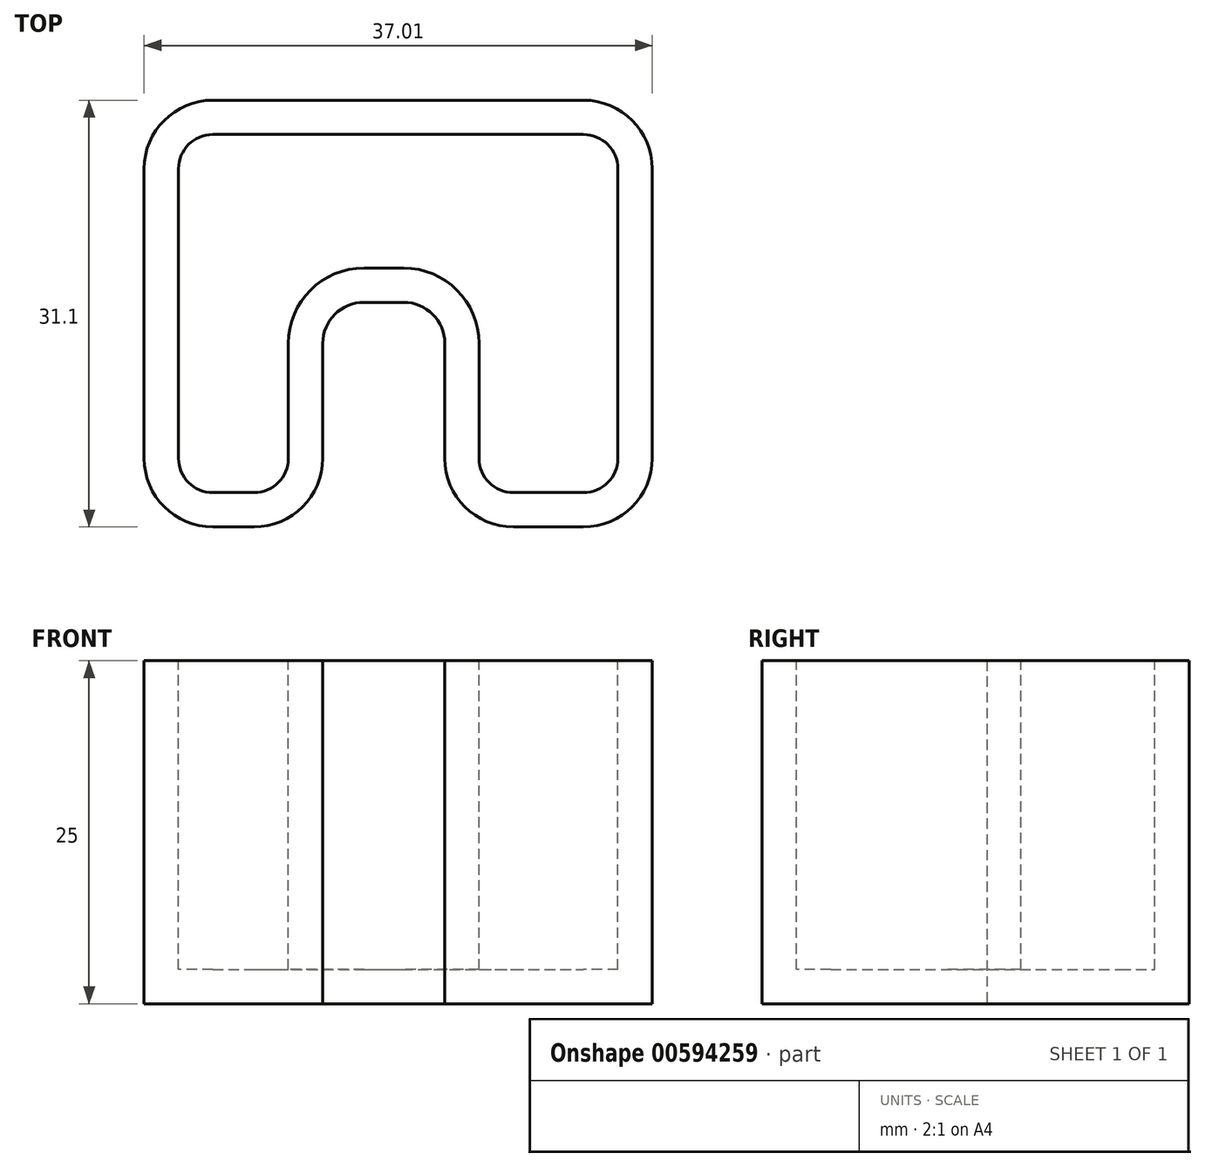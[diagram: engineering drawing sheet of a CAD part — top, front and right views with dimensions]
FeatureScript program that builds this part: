
annotation { "Feature Type Name" : "Feature", "Feature Type Description" : "" }
export const myFeature = defineFeature(function(context is Context, id is Id, definition is map)
    precondition{}
    {
        {
            var Q0;
            Q0=qCreatedBy(makeId("Top.planeOp"),FACE);
            var sketch = newSketch(context, id + "F0", { "sketchPlane" : qUnion([Q0])});
            skLineSegment(sketch, "E0.bottom", {"start": v(5, 0) * mm, "end": v(8, 0) * mm});
            skLineSegment(sketch, "E0.top", {"start": v(5, 31.1) * mm, "end": v(32, 31.1) * mm});
            skLineSegment(sketch, "E0.left", {"start": v(0, 5) * mm, "end": v(0, 26.1) * mm});
            skLineSegment(sketch, "E0.right", {"start": v(37, 5) * mm, "end": v(37, 26.1) * mm});
            skLineSegment(sketch, "E1.top", {"start": v(16, 16.37) * mm, "end": v(18.9, 16.37) * mm});
            skLineSegment(sketch, "E1.left", {"start": v(13, 5) * mm, "end": v(13, 13.37) * mm});
            skLineSegment(sketch, "E1.right", {"start": v(21.9, 5) * mm, "end": v(21.9, 13.37) * mm});
            skLineSegment(sketch, "E2.trimOffspring", {"start": v(26.9, 0) * mm, "end": v(32, 0) * mm});
            skPoint(sketch, "E3.visualSharp", {"position": v(0, 31.1) * mm});
            skArc(sketch, "E3.filletArc", {"start": v(5, 31.1) * mm, "mid": v(1.46, 29.63) * mm, "end": v(0, 26.1) * mm});
            skPoint(sketch, "E4.visualSharp", {"position": v(37, 31.1) * mm});
            skArc(sketch, "E4.filletArc", {"start": v(37, 26.1) * mm, "mid": v(35.54, 29.63) * mm, "end": v(32, 31.1) * mm});
            skPoint(sketch, "E5.visualSharp", {"position": v(37, 0) * mm});
            skArc(sketch, "E5.filletArc", {"start": v(32, 0) * mm, "mid": v(35.54, 1.46) * mm, "end": v(37, 5) * mm});
            skPoint(sketch, "E6.visualSharp", {"position": v(21.9, 0) * mm});
            skArc(sketch, "E6.filletArc", {"start": v(21.9, 5) * mm, "mid": v(23.36, 1.46) * mm, "end": v(26.9, 0) * mm});
            skPoint(sketch, "E7.visualSharp", {"position": v(21.9, 16.37) * mm});
            skArc(sketch, "E7.filletArc", {"start": v(21.9, 13.37) * mm, "mid": v(21.02, 15.49) * mm, "end": v(18.9, 16.37) * mm});
            skPoint(sketch, "E8.visualSharp", {"position": v(0, 0) * mm});
            skArc(sketch, "E8.filletArc", {"start": v(0, 5) * mm, "mid": v(1.46, 1.46) * mm, "end": v(5, 0) * mm});
            skPoint(sketch, "E9.visualSharp", {"position": v(13, 0) * mm});
            skArc(sketch, "E9.filletArc", {"start": v(8, 0) * mm, "mid": v(11.54, 1.46) * mm, "end": v(13, 5) * mm});
            skPoint(sketch, "E10.visualSharp", {"position": v(13, 16.37) * mm});
            skArc(sketch, "E10.filletArc", {"start": v(16, 16.37) * mm, "mid": v(13.89, 15.49) * mm, "end": v(13, 13.37) * mm});
            skSolve(sketch);
        }
        {
            var Q0;
            Q0 = qSketchRegion(id + "F0", true);
            extrude(context, id + "F1", {"entities" : qUnion([Q0]), "depth" : 25 * mm, "offsetDistance" : 25 * mm});
        }
        {
            var Q0;
            Q0=makeQuery(id+"F1.opExtrude","CAP_FACE",FACE,{"disambiguationData":[OSD([sQuery(id+"F0.wireOp",EDGE,"E0.bottom"),sQuery(id+"F0.wireOp",EDGE,"E0.top"),sQuery(id+"F0.wireOp",EDGE,"E0.left"),sQuery(id+"F0.wireOp",EDGE,"E0.right"),sQuery(id+"F0.wireOp",EDGE,"E1.top"),sQuery(id+"F0.wireOp",EDGE,"E1.left"),sQuery(id+"F0.wireOp",EDGE,"E1.right"),sQuery(id+"F0.wireOp",EDGE,"E2.trimOffspring"),sQuery(id+"F0.wireOp",EDGE,"E3.filletArc"),sQuery(id+"F0.wireOp",EDGE,"E4.filletArc"),sQuery(id+"F0.wireOp",EDGE,"E5.filletArc"),sQuery(id+"F0.wireOp",EDGE,"E6.filletArc"),sQuery(id+"F0.wireOp",EDGE,"E7.filletArc"),sQuery(id+"F0.wireOp",EDGE,"E8.filletArc"),sQuery(id+"F0.wireOp",EDGE,"E9.filletArc"),sQuery(id+"F0.wireOp",EDGE,"E10.filletArc")])],"isStart":false});
            shell(context, id + "F2", {"entities" : qUnion([Q0]), "thickness" : 2.5 * mm});
        }
    });
